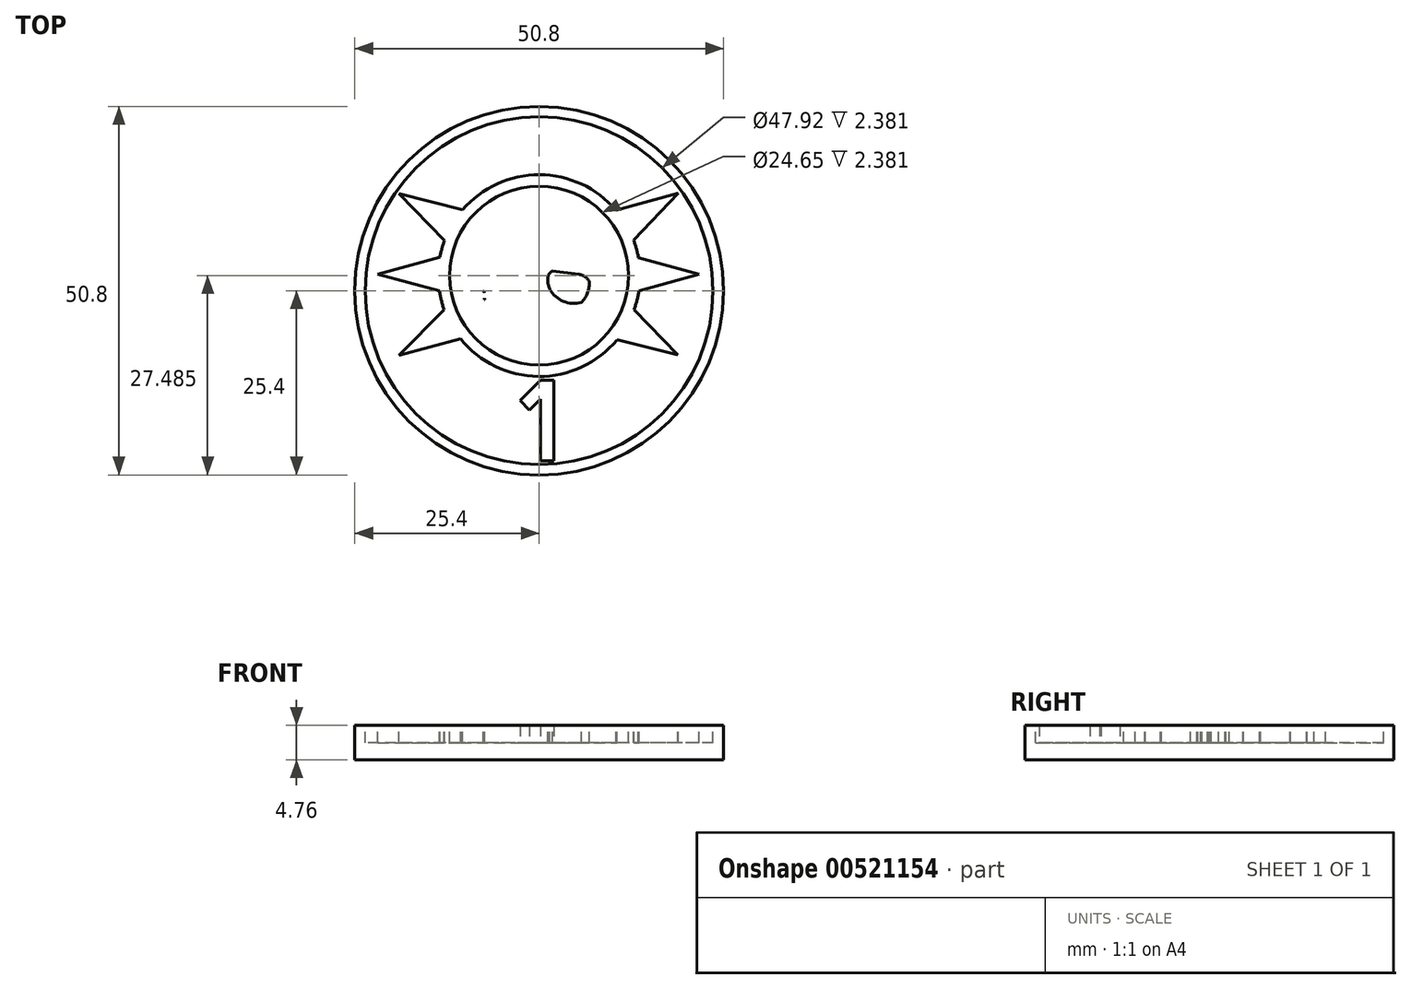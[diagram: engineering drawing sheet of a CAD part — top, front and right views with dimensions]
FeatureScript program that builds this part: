
annotation { "Feature Type Name" : "Feature", "Feature Type Description" : "" }
export const myFeature = defineFeature(function(context is Context, id is Id, definition is map)
    precondition{}
    {
        {
            var Q0;
            Q0=qCreatedBy(makeId("Top.planeOp"),FACE);
            var sketch = newSketch(context, id + "F0", { "sketchPlane" : qUnion([Q0])});
            skCircle(sketch, "E0", {"center": v(0, 0) * mm, "radius": 25.4 * mm});
            skSolve(sketch);
        }
        {
            var Q0;
            Q0=makeQuery(id+"F0.imprint","IMPRINT",FACE,{"disambiguationData":[TD([[makeQuery(id+"F0.imprint","IMPRINT",EDGE,{"derivedFrom":sQuery(id+"F0.wireOp",EDGE,"E0")}),1.0]])]});
            extrude(context, id + "F1", {"entities" : qUnion([Q0]), "depth" : 4.76 * mm, "offsetDistance" : 25.4 * mm});
        }
        {
            var Q0;
            Q0=makeQuery(id+"F1.opExtrude","CAP_FACE",FACE,{"disambiguationData":[OSD([sQuery(id+"F0.wireOp",EDGE,"E0")])],"isStart":false});
            var sketch = newSketch(context, id + "F2", { "sketchPlane" : qUnion([Q0])});
            skLineSegment(sketch, "E1", {"start": v(0, 0) * mm, "end": v(0, 25.4) * mm});
            skArc(sketch, "E2", {"start": v(-0.33, 11.95) * mm, "mid": v(-7.7, 8.08) * mm, "end": v(-7.55, -0.24) * mm});
            skLineSegment(sketch, "E3", {"start": v(-7.48, -1.06) * mm, "end": v(-7.73, -1.69) * mm});
            skArc(sketch, "E4", {"start": v(-7.55, -1.24) * mm, "mid": v(-7.44, -0.63) * mm, "end": v(-7.66, -0.06) * mm});
            skLineSegment(sketch, "E5", {"start": v(-6.9, -4.41) * mm, "end": v(-4.69, -4.62) * mm});
            skLineSegment(sketch, "E6", {"start": v(-4.56, -4.7) * mm, "end": v(-4.14, -5.5) * mm});
            skLineSegment(sketch, "E7", {"start": v(-4.12, -5.57) * mm, "end": v(-4.12, -6.26) * mm});
            skLineSegment(sketch, "E8", {"start": v(-3.62, -5.79) * mm, "end": v(-3.62, -6.3) * mm});
            skLineSegment(sketch, "E9", {"start": v(-3.22, -5.83) * mm, "end": v(-3.22, -6.7) * mm});
            skLineSegment(sketch, "E10", {"start": v(-2.5, -6.15) * mm, "end": v(-2.5, -6.76) * mm});
            skLineSegment(sketch, "E11", {"start": v(-1.96, -6.2) * mm, "end": v(-1.96, -7.04) * mm});
            skLineSegment(sketch, "E12", {"start": v(-1.28, -6.38) * mm, "end": v(-1.28, -7.15) * mm});
            skLineSegment(sketch, "E13", {"start": v(-0.76, -6.38) * mm, "end": v(-0.76, -7.25) * mm});
            skLineSegment(sketch, "E14", {"start": v(0, -6.43) * mm, "end": v(0, -7.2) * mm});
            skLineSegment(sketch, "E15", {"start": v(0.42, -6.43) * mm, "end": v(0.42, -7.2) * mm});
            skLineSegment(sketch, "E16", {"start": v(1.1, -6.35) * mm, "end": v(1.1, -7.2) * mm});
            skLineSegment(sketch, "E17", {"start": v(1.66, -6.3) * mm, "end": v(1.66, -6.98) * mm});
            skLineSegment(sketch, "E18", {"start": v(2.3, -6.14) * mm, "end": v(2.3, -6.97) * mm});
            skLineSegment(sketch, "E19", {"start": v(2.65, -6.1) * mm, "end": v(2.71, -6.42) * mm});
            skLineSegment(sketch, "E20", {"start": v(3.3, -5.72) * mm, "end": v(3.84, -4.99) * mm});
            skLineSegment(sketch, "E21", {"start": v(6.1, -4.92) * mm, "end": v(3.97, -4.92) * mm});
            skLineSegment(sketch, "E22", {"start": v(-5.43, 2.26) * mm, "end": v(-1.82, 2.72) * mm});
            skPoint(sketch, "E23", {"position": v(-6.9, 1.26) * mm});
            skPoint(sketch, "E24", {"position": v(-5.8, -1.59) * mm});
            skPoint(sketch, "E25", {"position": v(-1.48, 0.2) * mm});
            skPoint(sketch, "E26", {"position": v(-1.26, 2.12) * mm});
            skArc(sketch, "E27", {"start": v(-7.73, -1.69) * mm, "mid": v(-7.8, -3.16) * mm, "end": v(-6.97, -4.38) * mm});
            skPoint(sketch, "E28.visualSharp", {"position": v(-6.94, -4.4) * mm});
            skArc(sketch, "E28.filletArc", {"start": v(-6.97, -4.38) * mm, "mid": v(-6.93, -4.4) * mm, "end": v(-6.9, -4.41) * mm});
            skPoint(sketch, "E29.visualSharp", {"position": v(-4.6, -4.63) * mm});
            skArc(sketch, "E29.filletArc", {"start": v(-4.56, -4.7) * mm, "mid": v(-4.62, -4.65) * mm, "end": v(-4.69, -4.62) * mm});
            skArc(sketch, "E30", {"start": v(-5.43, 2.26) * mm, "mid": v(-6.29, 1.94) * mm, "end": v(-6.9, 1.26) * mm});
            skArc(sketch, "E31", {"start": v(-6.9, 1.26) * mm, "mid": v(-6.67, -0.28) * mm, "end": v(-5.8, -1.59) * mm});
            skArc(sketch, "E32", {"start": v(-1.48, 0.2) * mm, "mid": v(-1.2, 1.15) * mm, "end": v(-1.26, 2.12) * mm});
            skArc(sketch, "E33", {"start": v(-1.26, 2.12) * mm, "mid": v(-1.5, 2.46) * mm, "end": v(-1.82, 2.72) * mm});
            skArc(sketch, "E34", {"start": v(-5.8, -1.59) * mm, "mid": v(-3.33, -1.45) * mm, "end": v(-1.48, 0.2) * mm});
            skArc(sketch, "E35.MirrorCS", {"start": v(0.33, 11.95) * mm, "mid": v(7.7, 8.08) * mm, "end": v(7.55, -0.24) * mm});
            skArc(sketch, "E36.MirrorCS", {"start": v(5.43, 2.26) * mm, "mid": v(6.29, 1.94) * mm, "end": v(6.9, 1.26) * mm});
            skLineSegment(sketch, "E37.MirrorCS", {"start": v(5.43, 2.26) * mm, "end": v(1.82, 2.72) * mm});
            skArc(sketch, "E38.MirrorCS", {"start": v(1.26, 2.12) * mm, "mid": v(1.5, 2.46) * mm, "end": v(1.82, 2.72) * mm});
            skArc(sketch, "E39.MirrorCS", {"start": v(1.48, 0.2) * mm, "mid": v(1.2, 1.15) * mm, "end": v(1.26, 2.12) * mm});
            skArc(sketch, "E40.MirrorCS", {"start": v(5.8, -1.59) * mm, "mid": v(3.33, -1.45) * mm, "end": v(1.48, 0.2) * mm});
            skArc(sketch, "E41.MirrorCS", {"start": v(6.9, 1.26) * mm, "mid": v(6.67, -0.28) * mm, "end": v(5.8, -1.59) * mm});
            skPoint(sketch, "E42", {"position": v(7.37, -2.43) * mm});
            skArc(sketch, "E43", {"start": v(6.15, -4.91) * mm, "mid": v(7.22, -3.9) * mm, "end": v(7.37, -2.43) * mm});
            skArc(sketch, "E44", {"start": v(7.55, -0.24) * mm, "mid": v(7.04, -1.3) * mm, "end": v(7.37, -2.43) * mm});
            skArc(sketch, "E45", {"start": v(-0.29, -0.3) * mm, "mid": v(-0.58, -0.16) * mm, "end": v(-0.87, -0.3) * mm});
            skArc(sketch, "E46", {"start": v(-0.87, -0.3) * mm, "mid": v(-1.54, -1.45) * mm, "end": v(-1.95, -2.72) * mm});
            skArc(sketch, "E47", {"start": v(-1.95, -2.72) * mm, "mid": v(-1.93, -3.53) * mm, "end": v(-1.73, -4.31) * mm});
            skArc(sketch, "E48", {"start": v(-1.73, -4.31) * mm, "mid": v(-0.75, -4.14) * mm, "end": v(-0.11, -3.38) * mm});
            skLineSegment(sketch, "E49", {"start": v(-0.29, -0.3) * mm, "end": v(-0.08, -0.82) * mm});
            skLineSegment(sketch, "E50.MirrorCS", {"start": v(0.29, -0.3) * mm, "end": v(0.08, -0.82) * mm});
            skArc(sketch, "E51.MirrorCS", {"start": v(0.29, -0.3) * mm, "mid": v(0.58, -0.16) * mm, "end": v(0.87, -0.3) * mm});
            skArc(sketch, "E52.MirrorCS", {"start": v(0.87, -0.3) * mm, "mid": v(1.54, -1.45) * mm, "end": v(1.95, -2.72) * mm});
            skArc(sketch, "E53.MirrorCS", {"start": v(1.95, -2.72) * mm, "mid": v(1.93, -3.53) * mm, "end": v(1.73, -4.31) * mm});
            skArc(sketch, "E54.MirrorCS", {"start": v(1.73, -4.31) * mm, "mid": v(0.75, -4.14) * mm, "end": v(0.11, -3.38) * mm});
            skPoint(sketch, "E55", {"position": v(0, -1.04) * mm});
            skPoint(sketch, "E56", {"position": v(0, -3.17) * mm});
            skLineSegment(sketch, "E57", {"start": v(-0.11, -3.38) * mm, "end": v(0, -3.17) * mm});
            skLineSegment(sketch, "E58", {"start": v(0.11, -3.38) * mm, "end": v(0, -3.17) * mm});
            skLineSegment(sketch, "E59", {"start": v(-0.08, -0.82) * mm, "end": v(0, -1.04) * mm});
            skLineSegment(sketch, "E60", {"start": v(0.08, -0.82) * mm, "end": v(0, -1.04) * mm});
            skArc(sketch, "E61", {"start": v(-13.03, 6.93) * mm, "mid": v(-13.4, 5.8) * mm, "end": v(-13.66, 4.65) * mm});
            skLineSegment(sketch, "E62", {"start": v(-13.03, 6.93) * mm, "end": v(-19.34, 13.38) * mm});
            skLineSegment(sketch, "E63", {"start": v(-19.34, 13.38) * mm, "end": v(-10.54, 11.15) * mm});
            skLineSegment(sketch, "E64", {"start": v(-22.2, 2.3) * mm, "end": v(-13.66, 4.65) * mm});
            skLineSegment(sketch, "E65", {"start": v(-22.2, 2.3) * mm, "end": v(-13.74, 0) * mm});
            skLineSegment(sketch, "E66", {"start": v(-19.33, -8.88) * mm, "end": v(-13.09, -2.6) * mm});
            skLineSegment(sketch, "E67", {"start": v(-19.33, -8.88) * mm, "end": v(-10.83, -6.62) * mm});
            skLineSegment(sketch, "E68", {"start": v(19.09, -8.84) * mm, "end": v(10.7, -6.78) * mm});
            skLineSegment(sketch, "E69", {"start": v(19.09, -8.84) * mm, "end": v(13.08, -2.62) * mm});
            skLineSegment(sketch, "E70", {"start": v(22.04, 2.25) * mm, "end": v(13.74, 0) * mm});
            skLineSegment(sketch, "E71", {"start": v(22.04, 2.25) * mm, "end": v(13.67, 4.58) * mm});
            skLineSegment(sketch, "E72", {"start": v(19.17, 13.42) * mm, "end": v(13, 7) * mm});
            skLineSegment(sketch, "E73", {"start": v(19.17, 13.42) * mm, "end": v(10.58, 11.1) * mm});
            skArc(sketch, "E74.trimOffspring", {"start": v(-13.74, 0) * mm, "mid": v(-13.48, -1.31) * mm, "end": v(-13.09, -2.6) * mm});
            skArc(sketch, "E75.trimOffspring", {"start": v(-10.83, -6.62) * mm, "mid": v(-0.1, -11.82) * mm, "end": v(10.7, -6.78) * mm});
            skArc(sketch, "E76.trimOffspring", {"start": v(10.58, 11.1) * mm, "mid": v(0.03, 15.99) * mm, "end": v(-10.54, 11.15) * mm});
            skArc(sketch, "E77.trimOffspring", {"start": v(13.08, -2.62) * mm, "mid": v(13.48, -1.32) * mm, "end": v(13.74, 0) * mm});
            skArc(sketch, "E78.trimOffspring", {"start": v(13.67, 4.58) * mm, "mid": v(13.4, 5.8) * mm, "end": v(13, 7) * mm});
            skArc(sketch, "E79", {"start": v(-4.03, -6.4) * mm, "mid": v(-3.9, -6.44) * mm, "end": v(-3.77, -6.45) * mm});
            skArc(sketch, "E80", {"start": v(-3.2, -6.78) * mm, "mid": v(-2.9, -6.98) * mm, "end": v(-2.55, -6.87) * mm});
            skArc(sketch, "E81", {"start": v(-1.95, -7.1) * mm, "mid": v(-1.65, -7.34) * mm, "end": v(-1.29, -7.19) * mm});
            skArc(sketch, "E82", {"start": v(-0.64, -7.4) * mm, "mid": v(-0.36, -7.42) * mm, "end": v(-0.08, -7.34) * mm});
            skArc(sketch, "E83", {"start": v(0.45, -7.29) * mm, "mid": v(0.75, -7.45) * mm, "end": v(1.07, -7.3) * mm});
            skArc(sketch, "E84", {"start": v(1.7, -7.1) * mm, "mid": v(1.99, -7.21) * mm, "end": v(2.26, -7.07) * mm});
            skLineSegment(sketch, "E85", {"start": v(2.94, -6) * mm, "end": v(3.03, -6.42) * mm});
            skLineSegment(sketch, "E86", {"start": v(3.22, -5.78) * mm, "end": v(3.05, -5.82) * mm});
            skLineSegment(sketch, "E87", {"start": v(2.43, -5.98) * mm, "end": v(2.38, -6) * mm});
            skLineSegment(sketch, "E88", {"start": v(1.47, -6.15) * mm, "end": v(1.24, -6.2) * mm});
            skLineSegment(sketch, "E89", {"start": v(0.25, -6.27) * mm, "end": v(0.15, -6.28) * mm});
            skLineSegment(sketch, "E90", {"start": v(-0.9, -6.23) * mm, "end": v(-1.11, -6.22) * mm});
            skLineSegment(sketch, "E91", {"start": v(-2.1, -6.04) * mm, "end": v(-2.31, -6) * mm});
            skLineSegment(sketch, "E92", {"start": v(-3.31, -5.69) * mm, "end": v(-3.4, -5.65) * mm});
            skPoint(sketch, "E93.visualSharp", {"position": v(-0.76, -7.35) * mm});
            skArc(sketch, "E93.filletArc", {"start": v(-0.76, -7.25) * mm, "mid": v(-0.72, -7.34) * mm, "end": v(-0.64, -7.4) * mm});
            skPoint(sketch, "E94.visualSharp", {"position": v(0, -7.29) * mm});
            skArc(sketch, "E94.filletArc", {"start": v(-0.08, -7.34) * mm, "mid": v(-0.02, -7.28) * mm, "end": v(0, -7.2) * mm});
            skPoint(sketch, "E95.visualSharp", {"position": v(0.42, -7.24) * mm});
            skArc(sketch, "E95.filletArc", {"start": v(0.42, -7.2) * mm, "mid": v(0.43, -7.24) * mm, "end": v(0.45, -7.29) * mm});
            skPoint(sketch, "E96.visualSharp", {"position": v(1.1, -7.25) * mm});
            skArc(sketch, "E96.filletArc", {"start": v(1.07, -7.3) * mm, "mid": v(1.1, -7.26) * mm, "end": v(1.1, -7.2) * mm});
            skPoint(sketch, "E97.visualSharp", {"position": v(0.42, -6.26) * mm});
            skArc(sketch, "E97.filletArc", {"start": v(0.42, -6.43) * mm, "mid": v(0.37, -6.32) * mm, "end": v(0.25, -6.27) * mm});
            skPoint(sketch, "E98.visualSharp", {"position": v(0, -6.28) * mm});
            skArc(sketch, "E98.filletArc", {"start": v(0.15, -6.28) * mm, "mid": v(0.04, -6.32) * mm, "end": v(0, -6.43) * mm});
            skPoint(sketch, "E99.visualSharp", {"position": v(-1.28, -6.21) * mm});
            skArc(sketch, "E99.filletArc", {"start": v(-1.11, -6.22) * mm, "mid": v(-1.23, -6.26) * mm, "end": v(-1.28, -6.38) * mm});
            skPoint(sketch, "E100.visualSharp", {"position": v(-0.76, -6.23) * mm});
            skArc(sketch, "E100.filletArc", {"start": v(-0.76, -6.38) * mm, "mid": v(-0.8, -6.27) * mm, "end": v(-0.9, -6.23) * mm});
            skPoint(sketch, "E101.visualSharp", {"position": v(-1.96, -6.06) * mm});
            skArc(sketch, "E101.filletArc", {"start": v(-1.96, -6.2) * mm, "mid": v(-2, -6.1) * mm, "end": v(-2.1, -6.04) * mm});
            skPoint(sketch, "E102.visualSharp", {"position": v(-2.5, -5.96) * mm});
            skArc(sketch, "E102.filletArc", {"start": v(-2.31, -6) * mm, "mid": v(-2.44, -6.03) * mm, "end": v(-2.5, -6.15) * mm});
            skPoint(sketch, "E103.visualSharp", {"position": v(-3.22, -5.73) * mm});
            skArc(sketch, "E103.filletArc", {"start": v(-3.22, -5.83) * mm, "mid": v(-3.25, -5.74) * mm, "end": v(-3.31, -5.69) * mm});
            skPoint(sketch, "E104.visualSharp", {"position": v(-3.62, -5.54) * mm});
            skArc(sketch, "E104.filletArc", {"start": v(-3.4, -5.65) * mm, "mid": v(-3.55, -5.66) * mm, "end": v(-3.62, -5.79) * mm});
            skPoint(sketch, "E105.visualSharp", {"position": v(-4.12, -5.53) * mm});
            skArc(sketch, "E105.filletArc", {"start": v(-4.12, -5.57) * mm, "mid": v(-4.12, -5.53) * mm, "end": v(-4.14, -5.5) * mm});
            skPoint(sketch, "E106.visualSharp", {"position": v(-4.12, -6.35) * mm});
            skArc(sketch, "E106.filletArc", {"start": v(-4.12, -6.26) * mm, "mid": v(-4.1, -6.34) * mm, "end": v(-4.03, -6.4) * mm});
            skPoint(sketch, "E107.visualSharp", {"position": v(-3.62, -6.42) * mm});
            skArc(sketch, "E107.filletArc", {"start": v(-3.77, -6.45) * mm, "mid": v(-3.67, -6.4) * mm, "end": v(-3.62, -6.3) * mm});
            skPoint(sketch, "E108.visualSharp", {"position": v(-3.22, -6.73) * mm});
            skArc(sketch, "E108.filletArc", {"start": v(-3.22, -6.7) * mm, "mid": v(-3.22, -6.74) * mm, "end": v(-3.2, -6.78) * mm});
            skPoint(sketch, "E109.visualSharp", {"position": v(-2.5, -6.82) * mm});
            skArc(sketch, "E109.filletArc", {"start": v(-2.55, -6.87) * mm, "mid": v(-2.51, -6.82) * mm, "end": v(-2.5, -6.76) * mm});
            skPoint(sketch, "E110.visualSharp", {"position": v(-1.96, -7.07) * mm});
            skArc(sketch, "E110.filletArc", {"start": v(-1.96, -7.04) * mm, "mid": v(-1.96, -7.07) * mm, "end": v(-1.95, -7.1) * mm});
            skPoint(sketch, "E111.visualSharp", {"position": v(1.1, -6.21) * mm});
            skArc(sketch, "E111.filletArc", {"start": v(1.24, -6.2) * mm, "mid": v(1.14, -6.24) * mm, "end": v(1.1, -6.35) * mm});
            skPoint(sketch, "E112.visualSharp", {"position": v(1.66, -6.11) * mm});
            skArc(sketch, "E112.filletArc", {"start": v(1.66, -6.3) * mm, "mid": v(1.6, -6.18) * mm, "end": v(1.47, -6.15) * mm});
            skPoint(sketch, "E113.visualSharp", {"position": v(1.66, -7.04) * mm});
            skArc(sketch, "E113.filletArc", {"start": v(1.66, -6.98) * mm, "mid": v(1.67, -7.04) * mm, "end": v(1.7, -7.1) * mm});
            skPoint(sketch, "E114.visualSharp", {"position": v(2.3, -7.02) * mm});
            skArc(sketch, "E114.filletArc", {"start": v(2.26, -7.07) * mm, "mid": v(2.29, -7.02) * mm, "end": v(2.3, -6.97) * mm});
            skPoint(sketch, "E115.visualSharp", {"position": v(2.3, -6.05) * mm});
            skArc(sketch, "E115.filletArc", {"start": v(2.38, -6) * mm, "mid": v(2.32, -6.06) * mm, "end": v(2.3, -6.14) * mm});
            skPoint(sketch, "E116.visualSharp", {"position": v(2.62, -5.88) * mm});
            skArc(sketch, "E116.filletArc", {"start": v(2.65, -6.1) * mm, "mid": v(2.57, -5.98) * mm, "end": v(2.43, -5.98) * mm});
            skPoint(sketch, "E117.visualSharp", {"position": v(2.9, -5.85) * mm});
            skArc(sketch, "E117.filletArc", {"start": v(3.05, -5.82) * mm, "mid": v(2.96, -5.89) * mm, "end": v(2.94, -6) * mm});
            skPoint(sketch, "E118.visualSharp", {"position": v(3.27, -5.76) * mm});
            skArc(sketch, "E118.filletArc", {"start": v(3.22, -5.78) * mm, "mid": v(3.27, -5.75) * mm, "end": v(3.3, -5.72) * mm});
            skPoint(sketch, "E119.visualSharp", {"position": v(3.9, -4.92) * mm});
            skArc(sketch, "E119.filletArc", {"start": v(3.97, -4.92) * mm, "mid": v(3.9, -4.94) * mm, "end": v(3.84, -4.99) * mm});
            skPoint(sketch, "E120.visualSharp", {"position": v(6.12, -4.92) * mm});
            skArc(sketch, "E120.filletArc", {"start": v(6.1, -4.92) * mm, "mid": v(6.12, -4.92) * mm, "end": v(6.15, -4.91) * mm});
            skArc(sketch, "E121", {"start": v(2.93, -6.53) * mm, "mid": v(2.97, -6.51) * mm, "end": v(3, -6.48) * mm});
            skPoint(sketch, "E122.visualSharp", {"position": v(2.73, -6.53) * mm});
            skArc(sketch, "E122.filletArc", {"start": v(2.71, -6.42) * mm, "mid": v(2.8, -6.53) * mm, "end": v(2.93, -6.53) * mm});
            skPoint(sketch, "E123.visualSharp", {"position": v(3.03, -6.45) * mm});
            skArc(sketch, "E123.filletArc", {"start": v(3, -6.48) * mm, "mid": v(3.03, -6.45) * mm, "end": v(3.03, -6.42) * mm});
            skLineSegment(sketch, "E124", {"start": v(-0.33, 11.95) * mm, "end": v(0.33, 11.95) * mm});
            skPoint(sketch, "E125.orphan", {"position": v(0, 11.92) * mm});
            skCircle(sketch, "E126", {"center": v(0, 2.09) * mm, "radius": 12.32 * mm});
            skPoint(sketch, "E127.visualSharp", {"position": v(-1.28, -7.17) * mm});
            skArc(sketch, "E127.filletArc", {"start": v(-1.29, -7.19) * mm, "mid": v(-1.28, -7.17) * mm, "end": v(-1.28, -7.15) * mm});
            skCircle(sketch, "E128", {"center": v(0, 0) * mm, "radius": 23.96 * mm});
            skSolve(sketch);
        }
        {
            var Q0;
            Q0 = qSketchRegion(id + "F2", true);
            var Q1;
            Q1=makeQuery(id+"F2.imprint","IMPRINT",FACE,{"disambiguationData":[TD([[makeQuery(id+"F2.imprint","IMPRINT",EDGE,{"derivedFrom":sQuery(id+"F2.wireOp",EDGE,"E22")}),-1.0]])]});
            var Q2;
            Q2=makeQuery(id+"F2.imprint","IMPRINT",FACE,{"disambiguationData":[TD([[makeQuery(id+"F2.imprint","IMPRINT",EDGE,{"derivedFrom":sQuery(id+"F2.wireOp",EDGE,"E36.MirrorCS")}),-1.0]])]});
            var Q3;
            Q3=makeQuery(id+"F2.imprint","IMPRINT",FACE,{"disambiguationData":[TD([[makeQuery(id+"F2.imprint","IMPRINT",EDGE,{"derivedFrom":sQuery(id+"F2.wireOp",EDGE,"E5")}),-1.0]])]});
            var Q4;
            Q4=makeQuery(id+"F2.imprint","IMPRINT",FACE,{"disambiguationData":[TD([[makeQuery(id+"F2.imprint","IMPRINT",EDGE,{"derivedFrom":sQuery(id+"F2.wireOp",EDGE,"E45")}),1.0]])]});
            extrude(context, id + "F3", {"entities" : qUnion([Q0, Q1, Q2, Q3, Q4]), "operationType" : NewBodyOperationType.REMOVE, "oppositeDirection" : true, "depth" : 2.38 * mm, "offsetDistance" : 25.4 * mm});
        }
        {
            var Q0;
            Q0=makeQuery(id+"F3.boolean.opBoolean","COPY",FACE,{"derivedFrom":makeQuery(id+"F3.opExtrude","CAP_FACE",FACE,{"disambiguationData":[OSD([sQuery(id+"F2.wireOp",EDGE,"E61"),sQuery(id+"F2.wireOp",EDGE,"E62"),sQuery(id+"F2.wireOp",EDGE,"E63"),sQuery(id+"F2.wireOp",EDGE,"E64"),sQuery(id+"F2.wireOp",EDGE,"E65"),sQuery(id+"F2.wireOp",EDGE,"E66"),sQuery(id+"F2.wireOp",EDGE,"E67"),sQuery(id+"F2.wireOp",EDGE,"E68"),sQuery(id+"F2.wireOp",EDGE,"E69"),sQuery(id+"F2.wireOp",EDGE,"E70"),sQuery(id+"F2.wireOp",EDGE,"E71"),sQuery(id+"F2.wireOp",EDGE,"E72"),sQuery(id+"F2.wireOp",EDGE,"E73"),sQuery(id+"F2.wireOp",EDGE,"E74.trimOffspring"),sQuery(id+"F2.wireOp",EDGE,"E75.trimOffspring"),sQuery(id+"F2.wireOp",EDGE,"E76.trimOffspring"),sQuery(id+"F2.wireOp",EDGE,"E77.trimOffspring"),sQuery(id+"F2.wireOp",EDGE,"E78.trimOffspring"),sQuery(id+"F2.wireOp",EDGE,"E128")])],"isStart":false})});
            var sketch = newSketch(context, id + "F4", { "sketchPlane" : qUnion([Q0])});
            skText(sketch, "E129", { "text": "1", "fontName": "AllertaStencil-Regular.ttf"});
            skLineSegment(sketch, "E130", {"start": v(0, 0) * mm, "end": v(0, -27.58) * mm});
            const initialGuessF4  = {"E129": [-0.00306, -0.02343, 1, 0, 0.01111]};
            skSetInitialGuess(sketch, initialGuessF4);
            skSolve(sketch);
        }
        {
            var Q0;
            Q0 = qSketchRegion(id + "F4", true);
            extrude(context, id + "F5", {"entities" : qUnion([Q0]), "operationType" : NewBodyOperationType.ADD, "depth" : 2.38 * mm, "offsetDistance" : 25.4 * mm});
        }
    });
